# Revit family: LEGRAND_PRISES_VERROUILLEES_ENCASTREES_400
name_source: partatom
category: Installations électriques
revit_build: Autodesk Revit 2018 (Build: 20170223_1515(x64)
units: mm (PartAtom-declared; Revit-internal decimal feet)

## family parameters
Conserver l'orientation des annotations = Non
Cote de connecteur circulaire = Utiliser le diamètre
Couper avec des vides une fois chargée = Non
Hôte = Face
Partagée = Non
Point de calcul de pièce = Non
Type d'élément = Normal

## types (13) — shared parameters
A1 = Non
Conditions Générale d'Utilisation = https://export.legrand.com
Couleur caractéristique = rouge
Description = Prise verrouillée au standard international pour montage encastré ou saillie avec accessoire permet une connexion et déconnexion hors charge pour la sécurité des machines et des utilisateurs
Elévation par défaut = 1000 mm  [stored 3.28084 ft]
Fabricant = Legrand
Standard CEI ou NFC = CEI
Température maximale d'installation = 40°C
Température maximum d'utilisation = 100°C
Température minimum d'installation = -20°C
Température minimum d'utilisation = -20°C
Tension V = 400 V  50/60 Hz  rouge
Type de cerrouillage = verrouillage électromécanique
classe de protection IP = IP55
installation Encastrée E ou Saillie S = encastré et saillie

## per-type parameters (varying)
| type | Intensité A | Modèle | Nombre de pôles | Position de la Terre h | entraxe de fixation horizontal mm | entraxe de fixation vertical mm | hauteur mm | largeur mm | matériau du boitier | profondeur d'encastrement mm | profondeur mm | résistance aux chocs IK | sans halogène |
| Socle tableau Prisinter Hypra   IP44/55   16 A   380/415 V   2P+T   plast | 16 A | 052202 | 3 | 9 | 100 mm  [stored 0.328084 ft] | 100 mm  [stored 0.328084 ft] | 115 mm | 115 mm | plastique | 46 mm | 116 mm | 09 | Non |
| Socle tableau Prisinter Hypra   IP44/55   16 A   380/415 V   3P+N+T   métal | 16 A | 052214 | 5 | 6 | 110 mm | 110 mm | 125 mm | 125 mm | métal | 46 mm | 121 mm | 10 | Oui |
| Socle tableau Prisinter Hypra   IP44/55   16 A   380/415 V   3P+N+T   plast | 16 A | 052204 | 5 | 6 | 110 mm | 110 mm | 125 mm | 125 mm | plastique | 46 mm | 121 mm | 09 | Non |
| Socle tableau Prisinter Hypra   IP44/55   16 A   380/415 V   3P+T   métal | 16 A | 052213 | 4 | 6 | 100 mm  [stored 0.328084 ft] | 100 mm  [stored 0.328084 ft] | 115 mm | 115 mm | métal | 46 mm | 116 mm | 10 | Oui |
| Socle tableau Prisinter Hypra   IP44/55   16 A   380/415 V   3P+T   plast | 16 A | 052203 | 4 | 6 | 100 mm  [stored 0.328084 ft] | 100 mm  [stored 0.328084 ft] | 115 mm | 115 mm | plastique | 46 mm | 116 mm | 09 | Non |
| Socle tableau Prisinter Hypra   IP44/55   32 A   380/415 V   3P+N+T   métal | 32 A | 052914 | 5 | 6 | 125 mm | 125 mm | 143 mm | 143 mm | métal | 54 mm | 134 mm | 10 | Oui |
| Socle tableau Prisinter Hypra   IP44/55   32 A   380/415 V   3P+N+T   plast | 32 A | 052904 | 5 | 6 | 125 mm | 125 mm | 143 mm | 143 mm | plastique | 54 mm | 134 mm | 09 | Non |
| Socle tableau Prisinter Hypra   IP44/55   32 A   380/415 V   3P+T   métal | 32 A | 052913 | 4 | 6 | 125 mm | 125 mm | 143 mm | 143 mm | métal | 54 mm | 131 mm | 10 | Oui |
| Socle tableau Prisinter Hypra   IP44/55   32 A   380/415 V   3P+T   plast | 32 A | 052903 | 4 | 6 | 125 mm | 125 mm | 143 mm | 143 mm | plastique | 54 mm | 134 mm | 09 | Non |
| Socle tableau Prisinter Hypra   IP44/55   63 A   380/415 V   3P+N+T   métal | 63 A | 053801 | 5 | 6 | 125 mm | 125 mm | 143 mm | 143 mm | métal | 55 mm  [stored 0.180446 ft] | 154 mm  [stored 0.505249 ft] | 10 | Oui |
| Socle tableau Prisinter Hypra   IP44/55   63 A   380/415 V   3P+T   métal | 63 A | 053800 | 4 | 6 | 125 mm | 125 mm | 143 mm | 143 mm | métal | 55 mm  [stored 0.180446 ft] | 154 mm  [stored 0.505249 ft] | 10 | Oui |
| Socle tableau Prisinter Hypra IP44/55   63 A   380/415 V   3P+T   plast | 63 A | 053603 | 4 | 6 | 125 mm | 125 mm | 143 mm | 143 mm | plastique | 55 mm  [stored 0.180446 ft] | 154 mm  [stored 0.505249 ft] | 09 | Non |
| Socle tableau Prisinter Hypra IP44/55   63 A   380/415 V   3P+N+T   plast | 63 A | 053604 | 5 | 6 | 125 mm | 125 mm | 143 mm | 143 mm | plastique | 55 mm  [stored 0.180446 ft] | 154 mm  [stored 0.505249 ft] | 09 | Non |

note: [stored X ft] marks values corroborated as IEEE doubles in the binary element streams (Revit-internal decimal feet)
